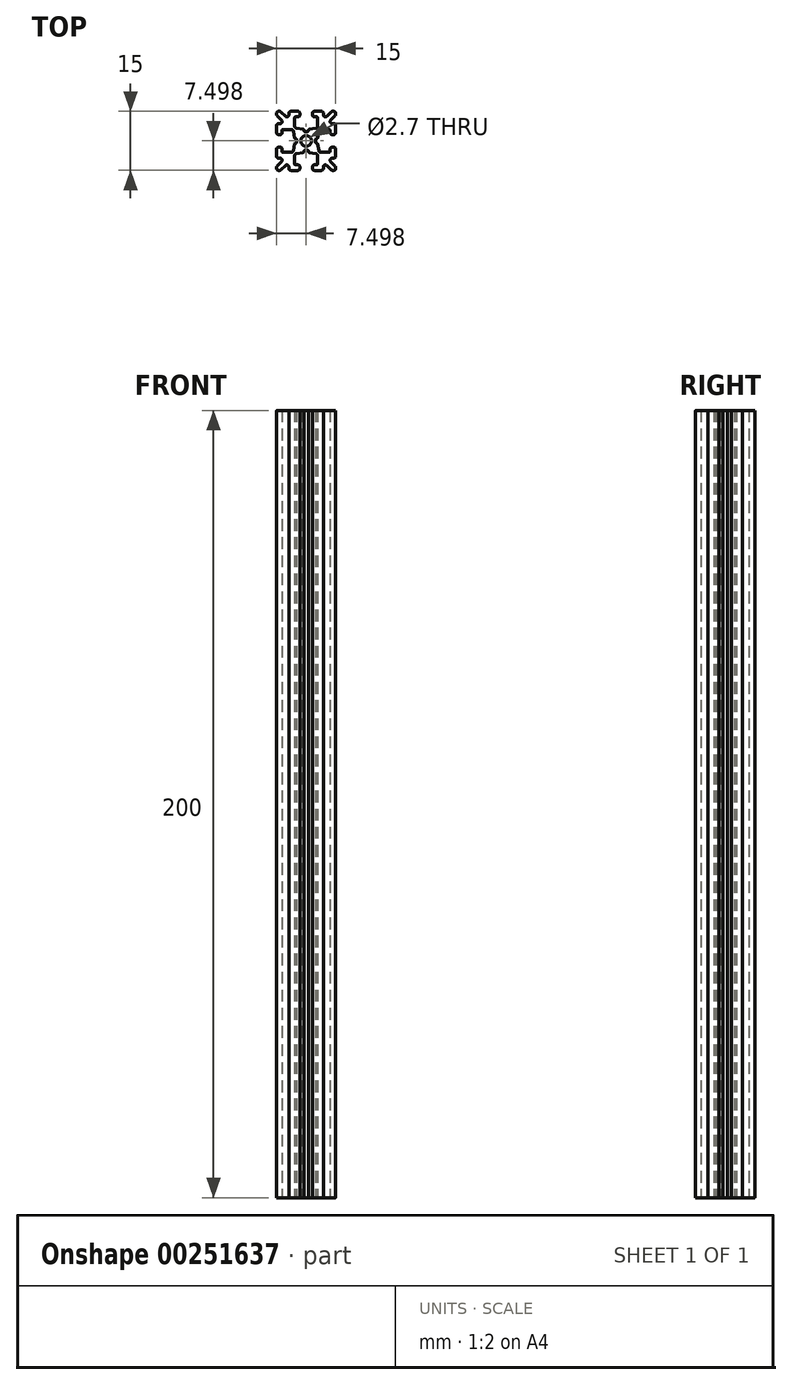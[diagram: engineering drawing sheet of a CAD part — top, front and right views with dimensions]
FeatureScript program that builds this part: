
annotation { "Feature Type Name" : "Feature", "Feature Type Description" : "" }
export const myFeature = defineFeature(function(context is Context, id is Id, definition is map)
    precondition{}
    {
        {
            var Q0;
            Q0=qCreatedBy(makeId("Top.planeOp"),FACE);
            var sketch = newSketch(context, id + "F0", { "sketchPlane" : qUnion([Q0])});
            skLineSegment(sketch, "E0", {"start": v(-28.06, 15.07) * mm, "end": v(-35.56, 7.57) * mm, "construction": true});
            skArc(sketch, "E1", {"start": v(-29.41, 15.07) * mm, "mid": v(-29.3, 14.55) * mm, "end": v(-29.02, 14.11) * mm});
            skLineSegment(sketch, "E2", {"start": v(-35.56, 8.07) * mm, "end": v(-35.56, 8.35) * mm});
            skLineSegment(sketch, "E3", {"start": v(-35.42, 8.7) * mm, "end": v(-34.3, 9.81) * mm});
            skLineSegment(sketch, "E4", {"start": v(-34.66, 10.66) * mm, "end": v(-35.06, 10.66) * mm});
            skLineSegment(sketch, "E5", {"start": v(-35.56, 11.16) * mm, "end": v(-35.56, 12.97) * mm});
            skLineSegment(sketch, "E6", {"start": v(-35.06, 13.47) * mm, "end": v(-34.66, 13.47) * mm});
            skLineSegment(sketch, "E7", {"start": v(-34.16, 12.97) * mm, "end": v(-34.16, 12.37) * mm});
            skLineSegment(sketch, "E8", {"start": v(-33.96, 12.17) * mm, "end": v(-31.8, 12.17) * mm});
            skLineSegment(sketch, "E9", {"start": v(-31.3, 12.58) * mm, "end": v(-31, 14.33) * mm});
            skLineSegment(sketch, "E10", {"start": v(-30.8, 14.5) * mm, "end": v(-30.66, 14.5) * mm});
            skLineSegment(sketch, "E11", {"start": v(-30.46, 14.7) * mm, "end": v(-30.46, 15.07) * mm});
            skLineSegment(sketch, "E12", {"start": v(-30.46, 15.07) * mm, "end": v(-29.41, 15.07) * mm, "construction": true});
            skPoint(sketch, "E13.visualSharp", {"position": v(-33.45, 10.66) * mm});
            skArc(sketch, "E13.filletArc", {"start": v(-34.3, 9.81) * mm, "mid": v(-34.2, 10.36) * mm, "end": v(-34.66, 10.66) * mm});
            skPoint(sketch, "E14.visualSharp", {"position": v(-34.16, 12.17) * mm});
            skArc(sketch, "E14.filletArc", {"start": v(-34.16, 12.37) * mm, "mid": v(-34.1, 12.23) * mm, "end": v(-33.96, 12.17) * mm});
            skPoint(sketch, "E15.visualSharp", {"position": v(-34.16, 13.47) * mm});
            skArc(sketch, "E15.filletArc", {"start": v(-34.16, 12.97) * mm, "mid": v(-34.3, 13.32) * mm, "end": v(-34.66, 13.47) * mm});
            skPoint(sketch, "E16.visualSharp", {"position": v(-35.56, 13.47) * mm});
            skArc(sketch, "E16.filletArc", {"start": v(-35.06, 13.47) * mm, "mid": v(-35.42, 13.32) * mm, "end": v(-35.56, 12.97) * mm});
            skPoint(sketch, "E17.visualSharp", {"position": v(-35.56, 10.66) * mm});
            skArc(sketch, "E17.filletArc", {"start": v(-35.56, 11.16) * mm, "mid": v(-35.42, 10.81) * mm, "end": v(-35.06, 10.66) * mm});
            skPoint(sketch, "E18.visualSharp", {"position": v(-35.56, 8.56) * mm});
            skArc(sketch, "E18.filletArc", {"start": v(-35.42, 8.7) * mm, "mid": v(-35.52, 8.54) * mm, "end": v(-35.56, 8.35) * mm});
            skPoint(sketch, "E19.visualSharp", {"position": v(-31.38, 12.17) * mm});
            skArc(sketch, "E19.filletArc", {"start": v(-31.8, 12.17) * mm, "mid": v(-31.48, 12.28) * mm, "end": v(-31.3, 12.58) * mm});
            skPoint(sketch, "E20.visualSharp", {"position": v(-30.96, 14.5) * mm});
            skArc(sketch, "E20.filletArc", {"start": v(-30.8, 14.5) * mm, "mid": v(-30.92, 14.45) * mm, "end": v(-31, 14.33) * mm});
            skPoint(sketch, "E21.visualSharp", {"position": v(-30.46, 14.5) * mm});
            skArc(sketch, "E21.filletArc", {"start": v(-30.66, 14.5) * mm, "mid": v(-30.52, 14.56) * mm, "end": v(-30.46, 14.7) * mm});
            skLineSegment(sketch, "E22.0.MirrorCS", {"start": v(-28.06, 12.67) * mm, "end": v(-28.06, 13.72) * mm, "construction": true});
            skPoint(sketch, "E22.1.MirrorP", {"position": v(-32.46, 7.57) * mm});
            skArc(sketch, "E22.2.MirrorCS", {"start": v(-34.43, 7.71) * mm, "mid": v(-34.59, 7.6) * mm, "end": v(-34.78, 7.57) * mm});
            skPoint(sketch, "E22.3.MirrorP", {"position": v(-29.66, 7.57) * mm});
            skArc(sketch, "E22.4.MirrorCS", {"start": v(-29.66, 8.07) * mm, "mid": v(-29.8, 7.71) * mm, "end": v(-30.16, 7.57) * mm});
            skArc(sketch, "E22.5.MirrorCS", {"start": v(-28.63, 12.33) * mm, "mid": v(-28.68, 12.2) * mm, "end": v(-28.8, 12.14) * mm});
            skPoint(sketch, "E22.6.MirrorP", {"position": v(-29.66, 8.97) * mm});
            skLineSegment(sketch, "E22.7.MirrorCS", {"start": v(-31.96, 7.57) * mm, "end": v(-30.16, 7.57) * mm});
            skArc(sketch, "E22.8.MirrorCS", {"start": v(-33.32, 8.82) * mm, "mid": v(-32.77, 8.93) * mm, "end": v(-32.46, 8.47) * mm});
            skPoint(sketch, "E22.9.MirrorP", {"position": v(-28.63, 12.67) * mm});
            skPoint(sketch, "E22.10.MirrorP", {"position": v(-32.46, 9.67) * mm});
            skArc(sketch, "E22.11.MirrorCS", {"start": v(-30.76, 8.97) * mm, "mid": v(-30.9, 9.03) * mm, "end": v(-30.96, 9.17) * mm});
            skPoint(sketch, "E22.12.MirrorP", {"position": v(-28.63, 12.17) * mm});
            skLineSegment(sketch, "E22.13.MirrorCS", {"start": v(-35.06, 7.57) * mm, "end": v(-34.78, 7.57) * mm});
            skLineSegment(sketch, "E22.14.MirrorCS", {"start": v(-29.66, 8.07) * mm, "end": v(-29.66, 8.47) * mm});
            skLineSegment(sketch, "E22.15.MirrorCS", {"start": v(-34.43, 7.71) * mm, "end": v(-33.32, 8.82) * mm});
            skArc(sketch, "E22.16.MirrorCS", {"start": v(-30.16, 8.97) * mm, "mid": v(-29.8, 8.82) * mm, "end": v(-29.66, 8.47) * mm});
            skLineSegment(sketch, "E22.17.MirrorCS", {"start": v(-32.46, 8.47) * mm, "end": v(-32.46, 8.07) * mm});
            skArc(sketch, "E22.18.MirrorCS", {"start": v(-30.96, 11.33) * mm, "mid": v(-30.85, 11.65) * mm, "end": v(-30.55, 11.82) * mm});
            skLineSegment(sketch, "E22.19.MirrorCS", {"start": v(-30.96, 9.17) * mm, "end": v(-30.96, 11.33) * mm});
            skLineSegment(sketch, "E22.20.MirrorCS", {"start": v(-30.16, 8.97) * mm, "end": v(-30.76, 8.97) * mm});
            skArc(sketch, "E22.21.MirrorCS", {"start": v(-28.63, 12.47) * mm, "mid": v(-28.57, 12.6) * mm, "end": v(-28.43, 12.67) * mm});
            skLineSegment(sketch, "E22.22.MirrorCS", {"start": v(-28.43, 12.67) * mm, "end": v(-28.06, 12.67) * mm});
            skPoint(sketch, "E22.23.MirrorP", {"position": v(-34.57, 7.57) * mm});
            skPoint(sketch, "E22.24.MirrorP", {"position": v(-30.96, 8.97) * mm});
            skLineSegment(sketch, "E22.25.MirrorCS", {"start": v(-30.55, 11.82) * mm, "end": v(-28.8, 12.14) * mm});
            skLineSegment(sketch, "E22.26.MirrorCS", {"start": v(-28.63, 12.33) * mm, "end": v(-28.63, 12.47) * mm});
            skArc(sketch, "E22.27.MirrorCS", {"start": v(-28.06, 13.72) * mm, "mid": v(-28.58, 13.82) * mm, "end": v(-29.02, 14.11) * mm});
            skArc(sketch, "E22.28.MirrorCS", {"start": v(-31.96, 7.57) * mm, "mid": v(-32.32, 7.71) * mm, "end": v(-32.46, 8.07) * mm});
            skPoint(sketch, "E22.29.MirrorP", {"position": v(-30.96, 11.75) * mm});
            skPoint(sketch, "E23.visualSharp", {"position": v(-35.56, 7.57) * mm});
            skArc(sketch, "E23.filletArc", {"start": v(-35.56, 8.07) * mm, "mid": v(-35.42, 7.71) * mm, "end": v(-35.06, 7.57) * mm});
            skLineSegment(sketch, "E24.0.MirrorCS", {"start": v(-28.06, 17.47) * mm, "end": v(-28.06, 16.42) * mm, "construction": true});
            skLineSegment(sketch, "E24.1.MirrorCS", {"start": v(-30.16, 21.17) * mm, "end": v(-30.76, 21.17) * mm});
            skLineSegment(sketch, "E24.2.MirrorCS", {"start": v(-35.56, 18.97) * mm, "end": v(-35.56, 17.17) * mm});
            skLineSegment(sketch, "E24.3.MirrorCS", {"start": v(-35.06, 16.67) * mm, "end": v(-34.66, 16.67) * mm});
            skArc(sketch, "E24.4.MirrorCS", {"start": v(-34.16, 17.17) * mm, "mid": v(-34.3, 16.81) * mm, "end": v(-34.66, 16.67) * mm});
            skPoint(sketch, "E24.5.MirrorP", {"position": v(-31.38, 17.97) * mm});
            skPoint(sketch, "E24.6.MirrorP", {"position": v(-28.63, 17.97) * mm});
            skArc(sketch, "E24.7.MirrorCS", {"start": v(-28.63, 17.67) * mm, "mid": v(-28.57, 17.53) * mm, "end": v(-28.43, 17.47) * mm});
            skArc(sketch, "E24.8.MirrorCS", {"start": v(-30.66, 15.64) * mm, "mid": v(-30.52, 15.58) * mm, "end": v(-30.46, 15.44) * mm});
            skLineSegment(sketch, "E24.9.MirrorCS", {"start": v(-28.43, 17.47) * mm, "end": v(-28.06, 17.47) * mm});
            skArc(sketch, "E24.10.MirrorCS", {"start": v(-34.16, 17.77) * mm, "mid": v(-34.1, 17.9) * mm, "end": v(-33.96, 17.97) * mm});
            skPoint(sketch, "E24.11.MirrorP", {"position": v(-32.46, 20.46) * mm});
            skLineSegment(sketch, "E24.12.MirrorCS", {"start": v(-30.96, 20.97) * mm, "end": v(-30.96, 18.8) * mm});
            skLineSegment(sketch, "E24.13.MirrorCS", {"start": v(-35.42, 21.43) * mm, "end": v(-34.3, 20.32) * mm});
            skPoint(sketch, "E24.14.MirrorP", {"position": v(-35.56, 21.58) * mm});
            skArc(sketch, "E24.15.MirrorCS", {"start": v(-31.8, 17.97) * mm, "mid": v(-31.48, 17.85) * mm, "end": v(-31.3, 17.56) * mm});
            skArc(sketch, "E24.16.MirrorCS", {"start": v(-30.16, 21.17) * mm, "mid": v(-29.8, 21.31) * mm, "end": v(-29.66, 21.67) * mm});
            skArc(sketch, "E24.17.MirrorCS", {"start": v(-35.06, 16.67) * mm, "mid": v(-35.42, 16.81) * mm, "end": v(-35.56, 17.17) * mm});
            skPoint(sketch, "E24.18.MirrorP", {"position": v(-29.66, 21.17) * mm});
            skPoint(sketch, "E24.19.MirrorP", {"position": v(-35.56, 19.47) * mm});
            skLineSegment(sketch, "E24.20.MirrorCS", {"start": v(-32.46, 21.67) * mm, "end": v(-32.46, 22.07) * mm});
            skArc(sketch, "E24.21.MirrorCS", {"start": v(-35.56, 18.97) * mm, "mid": v(-35.42, 19.32) * mm, "end": v(-35.06, 19.47) * mm});
            skPoint(sketch, "E24.22.MirrorP", {"position": v(-28.63, 17.47) * mm});
            skLineSegment(sketch, "E24.23.MirrorCS", {"start": v(-33.96, 17.97) * mm, "end": v(-31.8, 17.97) * mm});
            skArc(sketch, "E24.24.MirrorCS", {"start": v(-30.96, 18.8) * mm, "mid": v(-30.85, 18.48) * mm, "end": v(-30.55, 18.31) * mm});
            skArc(sketch, "E24.25.MirrorCS", {"start": v(-35.42, 21.43) * mm, "mid": v(-35.52, 21.6) * mm, "end": v(-35.56, 21.78) * mm});
            skPoint(sketch, "E24.26.MirrorP", {"position": v(-34.16, 17.97) * mm});
            skPoint(sketch, "E24.27.MirrorP", {"position": v(-32.46, 22.57) * mm});
            skArc(sketch, "E24.28.MirrorCS", {"start": v(-33.32, 21.31) * mm, "mid": v(-32.77, 21.2) * mm, "end": v(-32.46, 21.67) * mm});
            skArc(sketch, "E24.29.MirrorCS", {"start": v(-35.56, 22.07) * mm, "mid": v(-35.42, 22.42) * mm, "end": v(-35.06, 22.57) * mm});
            skPoint(sketch, "E24.30.MirrorP", {"position": v(-34.16, 16.67) * mm});
            skPoint(sketch, "E24.31.MirrorP", {"position": v(-30.96, 18.39) * mm});
            skPoint(sketch, "E24.32.MirrorP", {"position": v(-29.66, 22.57) * mm});
            skPoint(sketch, "E24.33.MirrorP", {"position": v(-30.96, 21.17) * mm});
            skLineSegment(sketch, "E24.34.MirrorCS", {"start": v(-31.96, 22.57) * mm, "end": v(-30.16, 22.57) * mm});
            skLineSegment(sketch, "E24.35.MirrorCS", {"start": v(-35.06, 22.57) * mm, "end": v(-34.78, 22.57) * mm});
            skArc(sketch, "E24.36.MirrorCS", {"start": v(-31.96, 22.57) * mm, "mid": v(-32.32, 22.42) * mm, "end": v(-32.46, 22.07) * mm});
            skPoint(sketch, "E24.37.MirrorP", {"position": v(-35.56, 22.57) * mm});
            skLineSegment(sketch, "E24.38.MirrorCS", {"start": v(-29.66, 22.07) * mm, "end": v(-29.66, 21.67) * mm});
            skLineSegment(sketch, "E24.39.MirrorCS", {"start": v(-34.43, 22.42) * mm, "end": v(-33.32, 21.31) * mm});
            skPoint(sketch, "E24.40.MirrorP", {"position": v(-35.56, 16.67) * mm});
            skArc(sketch, "E24.41.MirrorCS", {"start": v(-30.76, 21.17) * mm, "mid": v(-30.9, 21.1) * mm, "end": v(-30.96, 20.97) * mm});
            skArc(sketch, "E24.42.MirrorCS", {"start": v(-34.43, 22.42) * mm, "mid": v(-34.59, 22.53) * mm, "end": v(-34.78, 22.57) * mm});
            skLineSegment(sketch, "E24.43.MirrorCS", {"start": v(-30.55, 18.31) * mm, "end": v(-28.8, 18) * mm});
            skPoint(sketch, "E24.44.MirrorP", {"position": v(-30.96, 15.64) * mm});
            skLineSegment(sketch, "E24.45.MirrorCS", {"start": v(-34.66, 19.47) * mm, "end": v(-35.06, 19.47) * mm});
            skArc(sketch, "E24.46.MirrorCS", {"start": v(-29.66, 22.07) * mm, "mid": v(-29.8, 22.42) * mm, "end": v(-30.16, 22.57) * mm});
            skArc(sketch, "E24.47.MirrorCS", {"start": v(-30.8, 15.64) * mm, "mid": v(-30.92, 15.68) * mm, "end": v(-31, 15.8) * mm});
            skArc(sketch, "E24.48.MirrorCS", {"start": v(-34.3, 20.32) * mm, "mid": v(-34.2, 19.78) * mm, "end": v(-34.66, 19.47) * mm});
            skLineSegment(sketch, "E24.49.MirrorCS", {"start": v(-28.63, 17.8) * mm, "end": v(-28.63, 17.67) * mm});
            skLineSegment(sketch, "E24.50.MirrorCS", {"start": v(-30.8, 15.64) * mm, "end": v(-30.66, 15.64) * mm});
            skArc(sketch, "E24.51.MirrorCS", {"start": v(-29.41, 15.07) * mm, "mid": v(-29.3, 15.58) * mm, "end": v(-29.02, 16.02) * mm});
            skPoint(sketch, "E24.52.MirrorP", {"position": v(-30.46, 15.64) * mm});
            skPoint(sketch, "E24.53.MirrorP", {"position": v(-33.45, 19.47) * mm});
            skLineSegment(sketch, "E24.54.MirrorCS", {"start": v(-30.46, 15.44) * mm, "end": v(-30.46, 15.07) * mm});
            skArc(sketch, "E24.55.MirrorCS", {"start": v(-28.06, 16.42) * mm, "mid": v(-28.58, 16.31) * mm, "end": v(-29.02, 16.02) * mm});
            skLineSegment(sketch, "E24.56.MirrorCS", {"start": v(-31.3, 17.56) * mm, "end": v(-31, 15.8) * mm});
            skLineSegment(sketch, "E24.57.MirrorCS", {"start": v(-34.16, 17.17) * mm, "end": v(-34.16, 17.77) * mm});
            skLineSegment(sketch, "E24.58.MirrorCS", {"start": v(-35.56, 22.07) * mm, "end": v(-35.56, 21.78) * mm});
            skArc(sketch, "E24.59.MirrorCS", {"start": v(-28.63, 17.8) * mm, "mid": v(-28.68, 17.93) * mm, "end": v(-28.8, 18) * mm});
            skPoint(sketch, "E24.60.MirrorP", {"position": v(-34.57, 22.57) * mm});
            skLineSegment(sketch, "E25.0.MirrorCS", {"start": v(-21.06, 7.57) * mm, "end": v(-21.34, 7.57) * mm});
            skLineSegment(sketch, "E25.1.MirrorCS", {"start": v(-27.5, 17.8) * mm, "end": v(-27.5, 17.67) * mm});
            skLineSegment(sketch, "E25.2.MirrorCS", {"start": v(-27.7, 17.47) * mm, "end": v(-28.06, 17.47) * mm});
            skLineSegment(sketch, "E25.3.MirrorCS", {"start": v(-21.06, 22.57) * mm, "end": v(-21.34, 22.57) * mm});
            skLineSegment(sketch, "E25.4.MirrorCS", {"start": v(-26.46, 8.07) * mm, "end": v(-26.46, 8.47) * mm});
            skLineSegment(sketch, "E25.5.MirrorCS", {"start": v(-25.33, 15.64) * mm, "end": v(-25.46, 15.64) * mm});
            skLineSegment(sketch, "E25.6.MirrorCS", {"start": v(-21.06, 16.67) * mm, "end": v(-21.46, 16.67) * mm});
            skLineSegment(sketch, "E25.7.MirrorCS", {"start": v(-22.16, 17.97) * mm, "end": v(-24.32, 17.97) * mm});
            skLineSegment(sketch, "E25.8.MirrorCS", {"start": v(-20.7, 21.43) * mm, "end": v(-21.82, 20.32) * mm});
            skArc(sketch, "E25.9.MirrorCS", {"start": v(-25.36, 8.97) * mm, "mid": v(-25.22, 9.03) * mm, "end": v(-25.16, 9.17) * mm});
            skArc(sketch, "E25.10.MirrorCS", {"start": v(-25.16, 18.8) * mm, "mid": v(-25.28, 18.48) * mm, "end": v(-25.57, 18.31) * mm});
            skPoint(sketch, "E25.11.MirrorP", {"position": v(-26.46, 7.57) * mm});
            skPoint(sketch, "E25.12.MirrorP", {"position": v(-21.96, 13.47) * mm});
            skPoint(sketch, "E25.13.MirrorP", {"position": v(-25.16, 18.39) * mm});
            skPoint(sketch, "E25.14.MirrorP", {"position": v(-20.56, 13.47) * mm});
            skArc(sketch, "E25.15.MirrorCS", {"start": v(-26.46, 22.07) * mm, "mid": v(-26.32, 22.42) * mm, "end": v(-25.96, 22.57) * mm});
            skLineSegment(sketch, "E25.16.MirrorCS", {"start": v(-21.96, 12.97) * mm, "end": v(-21.96, 12.37) * mm});
            skLineSegment(sketch, "E25.17.MirrorCS", {"start": v(-25.66, 15.44) * mm, "end": v(-25.66, 15.07) * mm});
            skArc(sketch, "E25.18.MirrorCS", {"start": v(-21.06, 13.47) * mm, "mid": v(-20.7, 13.32) * mm, "end": v(-20.56, 12.97) * mm});
            skArc(sketch, "E25.19.MirrorCS", {"start": v(-20.56, 22.07) * mm, "mid": v(-20.7, 22.42) * mm, "end": v(-21.06, 22.57) * mm});
            skArc(sketch, "E25.20.MirrorCS", {"start": v(-25.96, 8.97) * mm, "mid": v(-26.32, 8.82) * mm, "end": v(-26.46, 8.47) * mm});
            skArc(sketch, "E25.21.MirrorCS", {"start": v(-21.96, 17.17) * mm, "mid": v(-21.82, 16.81) * mm, "end": v(-21.46, 16.67) * mm});
            skLineSegment(sketch, "E25.22.MirrorCS", {"start": v(-23.66, 21.67) * mm, "end": v(-23.66, 22.07) * mm});
            skLineSegment(sketch, "E25.23.MirrorCS", {"start": v(-21.46, 19.47) * mm, "end": v(-21.06, 19.47) * mm});
            skArc(sketch, "E25.24.MirrorCS", {"start": v(-21.06, 16.67) * mm, "mid": v(-20.7, 16.81) * mm, "end": v(-20.56, 17.17) * mm});
            skArc(sketch, "E25.25.MirrorCS", {"start": v(-28.06, 13.72) * mm, "mid": v(-27.55, 13.82) * mm, "end": v(-27.1, 14.11) * mm});
            skLineSegment(sketch, "E25.26.MirrorCS", {"start": v(-24.16, 7.57) * mm, "end": v(-25.96, 7.57) * mm});
            skLineSegment(sketch, "E25.27.MirrorCS", {"start": v(-25.96, 21.17) * mm, "end": v(-25.36, 21.17) * mm});
            skLineSegment(sketch, "E25.28.MirrorCS", {"start": v(-25.33, 14.5) * mm, "end": v(-25.46, 14.5) * mm});
            skLineSegment(sketch, "E25.29.MirrorCS", {"start": v(-23.66, 8.47) * mm, "end": v(-23.66, 8.07) * mm});
            skLineSegment(sketch, "E25.30.MirrorCS", {"start": v(-24.16, 22.57) * mm, "end": v(-25.96, 22.57) * mm});
            skArc(sketch, "E25.31.MirrorCS", {"start": v(-27.5, 12.33) * mm, "mid": v(-27.45, 12.2) * mm, "end": v(-27.33, 12.14) * mm});
            skArc(sketch, "E25.32.MirrorCS", {"start": v(-27.5, 17.67) * mm, "mid": v(-27.55, 17.53) * mm, "end": v(-27.7, 17.47) * mm});
            skPoint(sketch, "E25.33.MirrorP", {"position": v(-21.55, 7.57) * mm});
            skArc(sketch, "E25.34.MirrorCS", {"start": v(-24.16, 7.57) * mm, "mid": v(-23.8, 7.71) * mm, "end": v(-23.66, 8.07) * mm});
            skArc(sketch, "E25.35.MirrorCS", {"start": v(-25.36, 21.17) * mm, "mid": v(-25.22, 21.1) * mm, "end": v(-25.16, 20.97) * mm});
            skPoint(sketch, "E25.36.MirrorP", {"position": v(-27.5, 12.67) * mm});
            skPoint(sketch, "E25.37.MirrorP", {"position": v(-27.5, 17.97) * mm});
            skLineSegment(sketch, "E25.38.MirrorCS", {"start": v(-24.82, 12.58) * mm, "end": v(-25.13, 14.33) * mm});
            skPoint(sketch, "E25.39.MirrorP", {"position": v(-22.67, 10.66) * mm});
            skPoint(sketch, "E25.40.MirrorP", {"position": v(-25.66, 14.5) * mm});
            skLineSegment(sketch, "E25.41.MirrorCS", {"start": v(-20.56, 8.07) * mm, "end": v(-20.56, 8.35) * mm});
            skArc(sketch, "E25.42.MirrorCS", {"start": v(-20.7, 21.43) * mm, "mid": v(-20.6, 21.6) * mm, "end": v(-20.56, 21.78) * mm});
            skPoint(sketch, "E25.43.MirrorP", {"position": v(-23.66, 22.57) * mm});
            skArc(sketch, "E25.44.MirrorCS", {"start": v(-21.82, 20.32) * mm, "mid": v(-21.92, 19.78) * mm, "end": v(-21.46, 19.47) * mm});
            skPoint(sketch, "E25.45.MirrorP", {"position": v(-21.96, 12.17) * mm});
            skPoint(sketch, "E25.46.MirrorP", {"position": v(-23.66, 7.57) * mm});
            skArc(sketch, "E25.47.MirrorCS", {"start": v(-21.96, 17.77) * mm, "mid": v(-22.02, 17.9) * mm, "end": v(-22.16, 17.97) * mm});
            skLineSegment(sketch, "E25.48.MirrorCS", {"start": v(-25.96, 8.97) * mm, "end": v(-25.36, 8.97) * mm});
            skArc(sketch, "E25.49.MirrorCS", {"start": v(-25.33, 14.5) * mm, "mid": v(-25.2, 14.45) * mm, "end": v(-25.13, 14.33) * mm});
            skArc(sketch, "E25.50.MirrorCS", {"start": v(-20.7, 8.7) * mm, "mid": v(-20.6, 8.54) * mm, "end": v(-20.56, 8.35) * mm});
            skLineSegment(sketch, "E25.51.MirrorCS", {"start": v(-24.82, 17.56) * mm, "end": v(-25.13, 15.8) * mm});
            skArc(sketch, "E25.52.MirrorCS", {"start": v(-25.16, 11.33) * mm, "mid": v(-25.28, 11.65) * mm, "end": v(-25.57, 11.82) * mm});
            skArc(sketch, "E25.53.MirrorCS", {"start": v(-25.46, 15.64) * mm, "mid": v(-25.6, 15.58) * mm, "end": v(-25.66, 15.44) * mm});
            skPoint(sketch, "E25.54.MirrorP", {"position": v(-25.16, 15.64) * mm});
            skPoint(sketch, "E25.55.MirrorP", {"position": v(-20.56, 8.56) * mm});
            skLineSegment(sketch, "E25.56.MirrorCS", {"start": v(-25.57, 18.31) * mm, "end": v(-27.33, 18) * mm});
            skArc(sketch, "E25.57.MirrorCS", {"start": v(-26.46, 8.07) * mm, "mid": v(-26.32, 7.71) * mm, "end": v(-25.96, 7.57) * mm});
            skArc(sketch, "E25.58.MirrorCS", {"start": v(-25.96, 21.17) * mm, "mid": v(-26.32, 21.31) * mm, "end": v(-26.46, 21.67) * mm});
            skLineSegment(sketch, "E25.59.MirrorCS", {"start": v(-27.5, 12.33) * mm, "end": v(-27.5, 12.47) * mm});
            skLineSegment(sketch, "E25.60.MirrorCS", {"start": v(-25.66, 14.7) * mm, "end": v(-25.66, 15.07) * mm});
            skArc(sketch, "E25.61.MirrorCS", {"start": v(-20.56, 11.16) * mm, "mid": v(-20.7, 10.81) * mm, "end": v(-21.06, 10.66) * mm});
            skLineSegment(sketch, "E25.62.MirrorCS", {"start": v(-22.16, 12.17) * mm, "end": v(-24.32, 12.17) * mm});
            skLineSegment(sketch, "E25.63.MirrorCS", {"start": v(-20.56, 11.16) * mm, "end": v(-20.56, 12.97) * mm});
            skLineSegment(sketch, "E25.64.MirrorCS", {"start": v(-21.06, 13.47) * mm, "end": v(-21.46, 13.47) * mm});
            skArc(sketch, "E25.65.MirrorCS", {"start": v(-26.71, 15.07) * mm, "mid": v(-26.81, 14.55) * mm, "end": v(-27.1, 14.11) * mm});
            skPoint(sketch, "E25.66.MirrorP", {"position": v(-20.56, 16.67) * mm});
            skPoint(sketch, "E25.67.MirrorP", {"position": v(-26.46, 21.17) * mm});
            skLineSegment(sketch, "E25.68.MirrorCS", {"start": v(-21.7, 7.71) * mm, "end": v(-22.8, 8.82) * mm});
            skPoint(sketch, "E25.69.MirrorP", {"position": v(-25.66, 15.64) * mm});
            skPoint(sketch, "E25.70.MirrorP", {"position": v(-21.96, 16.67) * mm});
            skPoint(sketch, "E25.71.MirrorP", {"position": v(-24.74, 12.17) * mm});
            skPoint(sketch, "E25.72.MirrorP", {"position": v(-27.5, 12.17) * mm});
            skPoint(sketch, "E25.73.MirrorP", {"position": v(-20.56, 19.47) * mm});
            skArc(sketch, "E25.74.MirrorCS", {"start": v(-22.8, 8.82) * mm, "mid": v(-23.35, 8.93) * mm, "end": v(-23.66, 8.47) * mm});
            skArc(sketch, "E25.75.MirrorCS", {"start": v(-20.56, 8.07) * mm, "mid": v(-20.7, 7.71) * mm, "end": v(-21.06, 7.57) * mm});
            skLineSegment(sketch, "E25.76.MirrorCS", {"start": v(-25.57, 11.82) * mm, "end": v(-27.33, 12.14) * mm});
            skArc(sketch, "E25.77.MirrorCS", {"start": v(-24.32, 17.97) * mm, "mid": v(-24.64, 17.85) * mm, "end": v(-24.82, 17.56) * mm});
            skArc(sketch, "E25.78.MirrorCS", {"start": v(-21.7, 7.71) * mm, "mid": v(-21.54, 7.6) * mm, "end": v(-21.34, 7.57) * mm});
            skArc(sketch, "E25.79.MirrorCS", {"start": v(-20.56, 18.97) * mm, "mid": v(-20.7, 19.32) * mm, "end": v(-21.06, 19.47) * mm});
            skArc(sketch, "E25.80.MirrorCS", {"start": v(-25.33, 15.64) * mm, "mid": v(-25.2, 15.68) * mm, "end": v(-25.13, 15.8) * mm});
            skArc(sketch, "E25.81.MirrorCS", {"start": v(-21.7, 22.42) * mm, "mid": v(-21.54, 22.53) * mm, "end": v(-21.34, 22.57) * mm});
            skPoint(sketch, "E25.82.MirrorP", {"position": v(-23.66, 9.67) * mm});
            skPoint(sketch, "E25.83.MirrorP", {"position": v(-21.55, 22.57) * mm});
            skPoint(sketch, "E25.84.MirrorP", {"position": v(-25.16, 14.5) * mm});
            skLineSegment(sketch, "E25.85.MirrorCS", {"start": v(-25.16, 9.17) * mm, "end": v(-25.16, 11.33) * mm});
            skLineSegment(sketch, "E25.86.MirrorCS", {"start": v(-21.96, 17.17) * mm, "end": v(-21.96, 17.77) * mm});
            skLineSegment(sketch, "E25.87.MirrorCS", {"start": v(-21.7, 22.42) * mm, "end": v(-22.8, 21.31) * mm});
            skArc(sketch, "E25.88.MirrorCS", {"start": v(-27.5, 17.8) * mm, "mid": v(-27.45, 17.93) * mm, "end": v(-27.33, 18) * mm});
            skArc(sketch, "E25.89.MirrorCS", {"start": v(-27.5, 12.47) * mm, "mid": v(-27.55, 12.6) * mm, "end": v(-27.7, 12.67) * mm});
            skLineSegment(sketch, "E25.90.MirrorCS", {"start": v(-25.16, 20.97) * mm, "end": v(-25.16, 18.8) * mm});
            skArc(sketch, "E25.91.MirrorCS", {"start": v(-28.06, 16.42) * mm, "mid": v(-27.55, 16.31) * mm, "end": v(-27.1, 16.02) * mm});
            skArc(sketch, "E25.92.MirrorCS", {"start": v(-25.46, 14.5) * mm, "mid": v(-25.6, 14.56) * mm, "end": v(-25.66, 14.7) * mm});
            skPoint(sketch, "E25.93.MirrorP", {"position": v(-23.66, 20.46) * mm});
            skPoint(sketch, "E25.94.MirrorP", {"position": v(-25.16, 11.75) * mm});
            skPoint(sketch, "E25.95.MirrorP", {"position": v(-25.16, 21.17) * mm});
            skPoint(sketch, "E25.96.MirrorP", {"position": v(-22.67, 19.47) * mm});
            skPoint(sketch, "E25.97.MirrorP", {"position": v(-24.74, 17.97) * mm});
            skArc(sketch, "E25.98.MirrorCS", {"start": v(-24.32, 12.17) * mm, "mid": v(-24.64, 12.28) * mm, "end": v(-24.82, 12.58) * mm});
            skArc(sketch, "E25.99.MirrorCS", {"start": v(-24.16, 22.57) * mm, "mid": v(-23.8, 22.42) * mm, "end": v(-23.66, 22.07) * mm});
            skPoint(sketch, "E25.100.MirrorP", {"position": v(-20.56, 10.66) * mm});
            skPoint(sketch, "E25.101.MirrorP", {"position": v(-21.96, 17.97) * mm});
            skArc(sketch, "E25.102.MirrorCS", {"start": v(-26.71, 15.07) * mm, "mid": v(-26.81, 15.58) * mm, "end": v(-27.1, 16.02) * mm});
            skArc(sketch, "E25.103.MirrorCS", {"start": v(-22.8, 21.31) * mm, "mid": v(-23.35, 21.2) * mm, "end": v(-23.66, 21.67) * mm});
            skPoint(sketch, "E25.104.MirrorP", {"position": v(-20.56, 21.58) * mm});
            skPoint(sketch, "E25.105.MirrorP", {"position": v(-25.16, 8.97) * mm});
            skArc(sketch, "E25.106.MirrorCS", {"start": v(-21.82, 9.81) * mm, "mid": v(-21.92, 10.36) * mm, "end": v(-21.46, 10.66) * mm});
            skArc(sketch, "E25.107.MirrorCS", {"start": v(-21.96, 12.97) * mm, "mid": v(-21.82, 13.32) * mm, "end": v(-21.46, 13.47) * mm});
            skPoint(sketch, "E25.108.MirrorP", {"position": v(-26.46, 22.57) * mm});
            skPoint(sketch, "E25.109.MirrorP", {"position": v(-20.56, 22.57) * mm});
            skLineSegment(sketch, "E25.110.MirrorCS", {"start": v(-27.7, 12.67) * mm, "end": v(-28.06, 12.67) * mm});
            skPoint(sketch, "E25.111.MirrorP", {"position": v(-20.56, 7.57) * mm});
            skLineSegment(sketch, "E25.112.MirrorCS", {"start": v(-20.56, 22.07) * mm, "end": v(-20.56, 21.78) * mm});
            skArc(sketch, "E25.113.MirrorCS", {"start": v(-21.96, 12.37) * mm, "mid": v(-22.02, 12.23) * mm, "end": v(-22.16, 12.17) * mm});
            skLineSegment(sketch, "E25.114.MirrorCS", {"start": v(-26.46, 22.07) * mm, "end": v(-26.46, 21.67) * mm});
            skPoint(sketch, "E25.115.MirrorP", {"position": v(-26.46, 8.97) * mm});
            skLineSegment(sketch, "E25.116.MirrorCS", {"start": v(-20.7, 8.7) * mm, "end": v(-21.82, 9.81) * mm});
            skLineSegment(sketch, "E25.117.MirrorCS", {"start": v(-20.56, 18.97) * mm, "end": v(-20.56, 17.17) * mm});
            skPoint(sketch, "E25.118.MirrorP", {"position": v(-27.5, 17.47) * mm});
            skLineSegment(sketch, "E25.119.MirrorCS", {"start": v(-21.46, 10.66) * mm, "end": v(-21.06, 10.66) * mm});
            skSolve(sketch);
        }
        {
            var Q0;
            Q0=makeQuery(id+"F0.imprint","IMPRINT",FACE,{"disambiguationData":[TD([[makeQuery(id+"F0.imprint","IMPRINT",EDGE,{"derivedFrom":sQuery(id+"F0.wireOp",EDGE,"E1")}),-1.0]])]});
            extrude(context, id + "F1", {"entities" : qUnion([Q0]), "depth" : 200 * mm});
        }
    });
